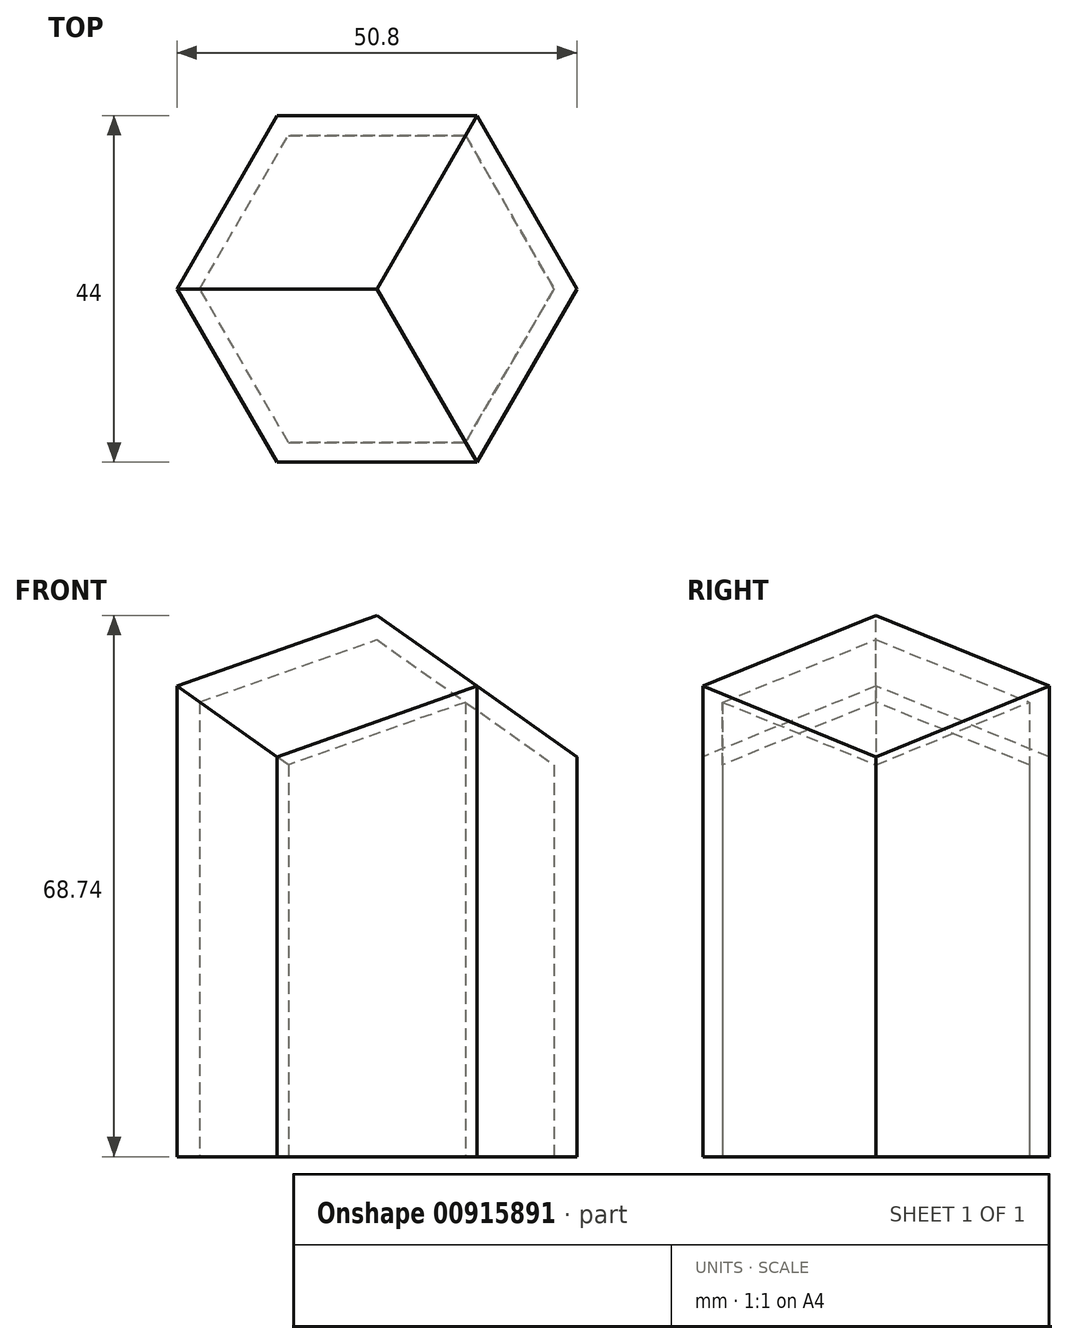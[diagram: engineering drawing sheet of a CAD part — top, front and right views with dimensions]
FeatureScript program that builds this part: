
annotation { "Feature Type Name" : "Feature", "Feature Type Description" : "" }
export const myFeature = defineFeature(function(context is Context, id is Id, definition is map)
    precondition{}
    {
        {
            var Q0;
            Q0=qCreatedBy(makeId("Top.planeOp"),FACE);
            var sketch = newSketch(context, id + "F0", { "sketchPlane" : qUnion([Q0])});
            skCircle(sketch, "E0.cCircle", {"center": v(0, 0) * mm, "radius": 22 * mm, "construction": true});
            skLineSegment(sketch, "E0.0", {"start": v(-12.7, 22) * mm, "end": v(12.7, 22) * mm});
            skLineSegment(sketch, "E0.1", {"start": v(12.7, 22) * mm, "end": v(25.4, 0) * mm});
            skLineSegment(sketch, "E0.2", {"start": v(25.4, 0) * mm, "end": v(12.7, -22) * mm});
            skLineSegment(sketch, "E0.3", {"start": v(12.7, -22) * mm, "end": v(-12.7, -22) * mm});
            skLineSegment(sketch, "E0.4", {"start": v(-12.7, -22) * mm, "end": v(-25.4, 0) * mm});
            skLineSegment(sketch, "E0.5", {"start": v(-25.4, 0) * mm, "end": v(-12.7, 22) * mm});
            skPoint(sketch, "E0.0.midPoint", {"position": v(0, 22) * mm});
            skSolve(sketch);
        }
        {
            var Q0;
            Q0=makeQuery(id+"F0.imprint","IMPRINT",FACE,{"disambiguationData":[TD([[makeQuery(id+"F0.imprint","IMPRINT",EDGE,{"derivedFrom":sQuery(id+"F0.wireOp",EDGE,"E0.0")}),-1.0]])]});
            extrude(context, id + "F1", {"entities" : qUnion([Q0]), "endBound" : BoundingType.SYMMETRIC, "depth" : 76.2 * mm, "offsetDistance" : 25.4 * mm});
        }
        {
            var Q0;
            Q0=makeQuery(id+"F1.opExtrude","SWEPT_FACE",FACE,{"disambiguationData":[OSD([sQuery(id+"F0.wireOp",EDGE,"E0.4")])]});
            var sketch = newSketch(context, id + "F2", { "sketchPlane" : qUnion([Q0])});
            skPoint(sketch, "E1", {"position": v(-12.7, 21.68) * mm});
            skPoint(sketch, "E2", {"position": v(12.7, 12.7) * mm});
            skSolve(sketch);
        }
        {
            var Q0;
            Q0=makeQuery(id+"F1.opExtrude","SWEPT_FACE",FACE,{"disambiguationData":[OSD([sQuery(id+"F0.wireOp",EDGE,"E0.2")])]});
            var sketch = newSketch(context, id + "F3", { "sketchPlane" : qUnion([Q0])});
            skPoint(sketch, "E3", {"position": v(-12.7, 21.67) * mm});
            skPoint(sketch, "E4", {"position": v(12.7, 12.7) * mm});
            skSolve(sketch);
        }
        {
            var Q0;
            Q0=makeQuery(id+"F1.opExtrude","SWEPT_FACE",FACE,{"disambiguationData":[OSD([sQuery(id+"F0.wireOp",EDGE,"E0.0")])]});
            var sketch = newSketch(context, id + "F4", { "sketchPlane" : qUnion([Q0])});
            skPoint(sketch, "E5", {"position": v(-12.7, 21.67) * mm});
            skPoint(sketch, "E6", {"position": v(12.7, 12.7) * mm});
            skSolve(sketch);
        }
        {
            var Q0;
            Q0=sQuery(id+"F4.wireOp",VERTEX,"E5");
            var Q1;
            Q1=sQuery(id+"F4.wireOp",VERTEX,"E6");
            var Q2;
            Q2=sQuery(id+"F2.wireOp",VERTEX,"E1");
            cPlane(context, id + "F5", {"entities" : qUnion([Q0, Q1, Q2]), "cplaneType" : CPlaneType.THREE_POINT, "offset" : 25.4 * mm, "width" : 152.4 * mm, "height" : 152.4 * mm});
        }
        {
            var Q0;
            Q0=sQuery(id+"F2.wireOp",VERTEX,"E1");
            var Q1;
            Q1=sQuery(id+"F2.wireOp",VERTEX,"E2");
            var Q2;
            Q2=sQuery(id+"F3.wireOp",VERTEX,"E3");
            cPlane(context, id + "F6", {"entities" : qUnion([Q0, Q1, Q2]), "cplaneType" : CPlaneType.THREE_POINT, "offset" : 25.4 * mm, "width" : 152.4 * mm, "height" : 152.4 * mm});
        }
        {
            var Q0;
            Q0=sQuery(id+"F3.wireOp",VERTEX,"E3");
            var Q1;
            Q1=sQuery(id+"F3.wireOp",VERTEX,"E4");
            var Q2;
            Q2=sQuery(id+"F4.wireOp",VERTEX,"E5");
            cPlane(context, id + "F7", {"entities" : qUnion([Q0, Q1, Q2]), "cplaneType" : CPlaneType.THREE_POINT, "offset" : 25.4 * mm, "width" : 152.4 * mm, "height" : 152.4 * mm});
        }
        {
            var Q0;
            Q0=qCreatedBy(id+"F5.planeOp",FACE);
            var sketch = newSketch(context, id + "F8", { "sketchPlane" : qUnion([Q0])});
            skLineSegment(sketch, "E7.bottom", {"start": v(-26.23, -22) * mm, "end": v(35.9, -22) * mm});
            skLineSegment(sketch, "E7.top", {"start": v(-26.23, 49) * mm, "end": v(35.9, 49) * mm});
            skLineSegment(sketch, "E7.left", {"start": v(-26.23, -22) * mm, "end": v(-26.23, 49) * mm});
            skLineSegment(sketch, "E7.right", {"start": v(35.9, -22) * mm, "end": v(35.9, 49) * mm});
            skSolve(sketch);
        }
        {
            var Q0;
            Q0=makeQuery(id+"F8.imprint","IMPRINT",FACE,{"disambiguationData":[TD([[makeQuery(id+"F8.imprint","IMPRINT",EDGE,{"derivedFrom":sQuery(id+"F8.wireOp",EDGE,"E7.bottom")}),1.0]])]});
            extrude(context, id + "F9", {"entities" : qUnion([Q0]), "operationType" : NewBodyOperationType.REMOVE, "endBound" : BoundingType.THROUGH_ALL, "oppositeDirection" : true, "depth" : 25.4 * mm, "offsetDistance" : 25.4 * mm});
        }
        {
            var Q0;
            Q0=qCreatedBy(id+"F6.planeOp",FACE);
            var sketch = newSketch(context, id + "F10", { "sketchPlane" : qUnion([Q0])});
            skLineSegment(sketch, "E8.bottom", {"start": v(-46.25, 48.56) * mm, "end": v(48.18, 48.56) * mm});
            skLineSegment(sketch, "E8.top", {"start": v(-46.25, -47.16) * mm, "end": v(48.18, -47.16) * mm});
            skLineSegment(sketch, "E8.left", {"start": v(-46.25, 48.56) * mm, "end": v(-46.25, -47.16) * mm});
            skLineSegment(sketch, "E8.right", {"start": v(48.18, 48.56) * mm, "end": v(48.18, -47.16) * mm});
            skSolve(sketch);
        }
        {
            var Q0;
            Q0=makeQuery(id+"F10.imprint","IMPRINT",FACE,{"disambiguationData":[TD([[makeQuery(id+"F10.imprint","IMPRINT",EDGE,{"derivedFrom":sQuery(id+"F10.wireOp",EDGE,"E8.bottom")}),-1.0]])]});
            extrude(context, id + "F11", {"entities" : qUnion([Q0]), "operationType" : NewBodyOperationType.REMOVE, "endBound" : BoundingType.THROUGH_ALL, "oppositeDirection" : true, "depth" : 25.4 * mm, "offsetDistance" : 25.4 * mm});
        }
        {
            var Q0;
            Q0=qCreatedBy(id+"F7.planeOp",FACE);
            var sketch = newSketch(context, id + "F12", { "sketchPlane" : qUnion([Q0])});
            skLineSegment(sketch, "E9.bottom", {"start": v(-35.38, 32.81) * mm, "end": v(46.48, 32.81) * mm});
            skLineSegment(sketch, "E9.top", {"start": v(-35.38, -34.33) * mm, "end": v(46.48, -34.33) * mm});
            skLineSegment(sketch, "E9.left", {"start": v(-35.38, 32.81) * mm, "end": v(-35.38, -34.33) * mm});
            skLineSegment(sketch, "E9.right", {"start": v(46.48, 32.81) * mm, "end": v(46.48, -34.33) * mm});
            skSolve(sketch);
        }
        {
            var Q0;
            Q0=makeQuery(id+"F12.imprint","IMPRINT",FACE,{"disambiguationData":[TD([[makeQuery(id+"F12.imprint","IMPRINT",EDGE,{"derivedFrom":sQuery(id+"F12.wireOp",EDGE,"E9.bottom")}),-1.0]])]});
            extrude(context, id + "F13", {"entities" : qUnion([Q0]), "operationType" : NewBodyOperationType.REMOVE, "endBound" : BoundingType.THROUGH_ALL, "oppositeDirection" : true, "depth" : 25.4 * mm, "offsetDistance" : 25.4 * mm});
        }
        {
            var Q0;
            Q0=makeQuery(id+"F1.opExtrude","CAP_FACE",FACE,{"disambiguationData":[OSD([sQuery(id+"F0.wireOp",EDGE,"E0.0"),sQuery(id+"F0.wireOp",EDGE,"E0.1"),sQuery(id+"F0.wireOp",EDGE,"E0.2"),sQuery(id+"F0.wireOp",EDGE,"E0.3"),sQuery(id+"F0.wireOp",EDGE,"E0.4"),sQuery(id+"F0.wireOp",EDGE,"E0.5")])],"isStart":true});
            shell(context, id + "F14", {"entities" : qUnion([Q0]), "thickness" : 2.5 * mm});
        }
    });
